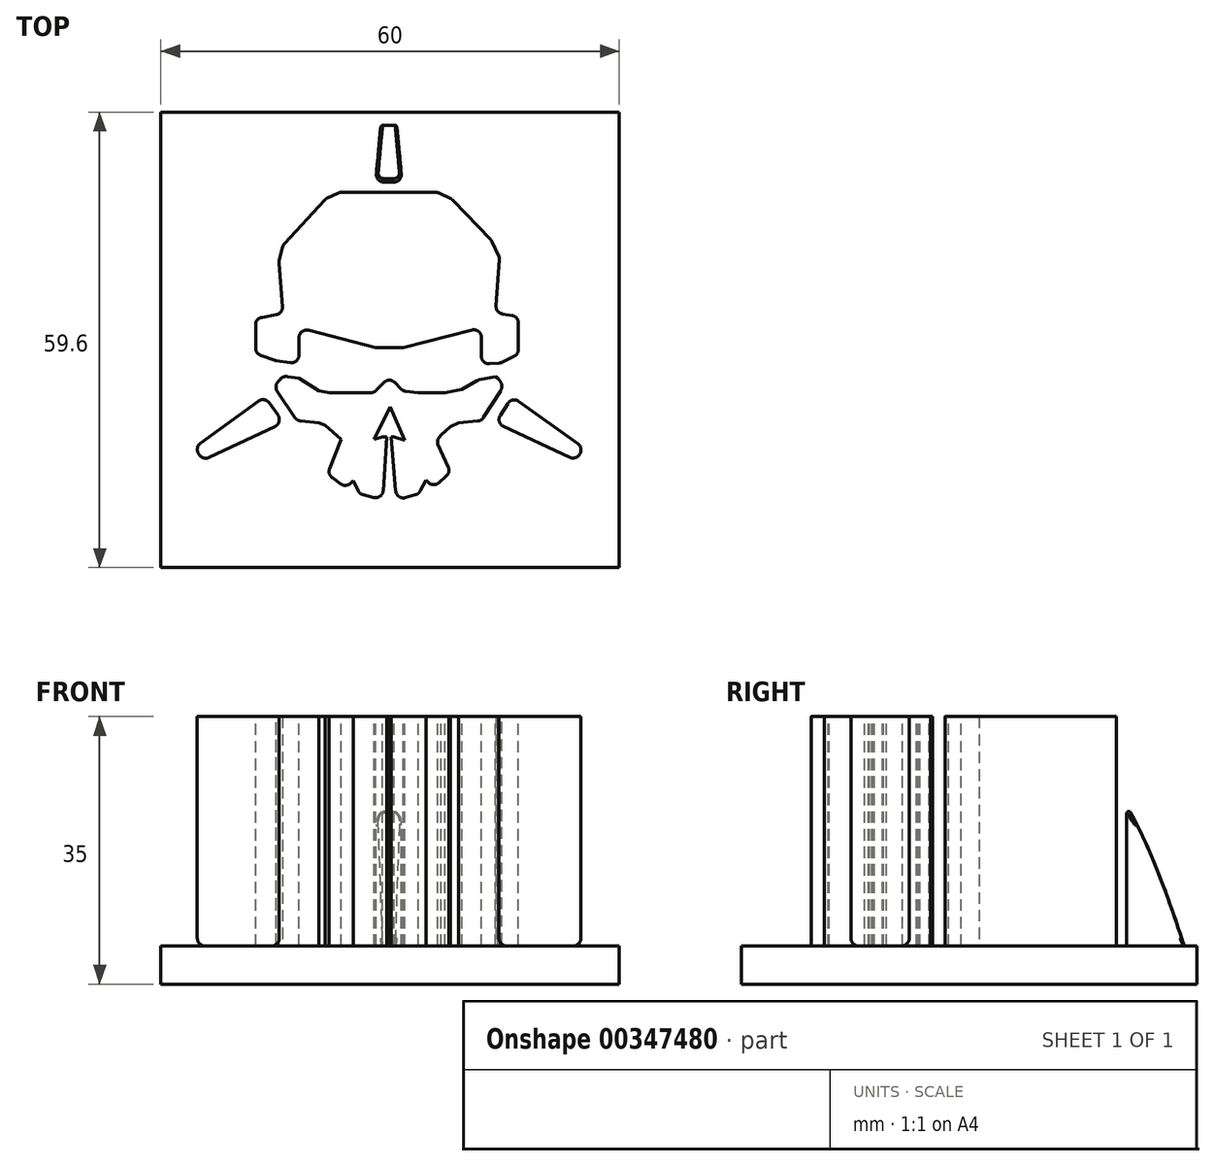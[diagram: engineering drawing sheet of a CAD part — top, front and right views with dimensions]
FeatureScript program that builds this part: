
annotation { "Feature Type Name" : "Feature", "Feature Type Description" : "" }
export const myFeature = defineFeature(function(context is Context, id is Id, definition is map)
    precondition{}
    {
        {
            var Q0;
            Q0=qCreatedBy(makeId("Front.planeOp"),FACE);
            var sketch = newSketch(context, id + "F0", { "sketchPlane" : qUnion([Q0])});
            skLineSegment(sketch, "E0", {"start": v(0, 0) * mm, "end": v(24, 0) * mm});
            skLineSegment(sketch, "E1", {"start": v(27, 5) * mm, "end": v(24, 0) * mm});
            skLineSegment(sketch, "E2", {"start": v(27, 5) * mm, "end": v(28.5, 5) * mm});
            skLineSegment(sketch, "E3", {"start": v(0, 35) * mm, "end": v(0, 0) * mm});
            skFitSpline(sketch, "E4", {"points": [v(0, 35) * mm, v(9.06, 34) * mm, v(13.03, 32.01) * mm, v(20.35, 24.23) * mm, v(28.5, 5) * mm], "startDerivative": vector(43.74, -2.76) * mm, "endDerivative": vector(20.52, -60.26) * mm});
            skSolve(sketch);
        }
        {
            var Q0;
            Q0=qSketchRegion(id+"F0",true);
            var Q1;
            Q1=sQuery(id+"F0.wireOp",EDGE,"E3");
            revolve(context, id + "F1", {"entities" : qUnion([Q0]), "axis" : qUnion([Q1]), "revolveType" : RevolveType.FULL});
        }
        {
            var Q0;
            Q0=qCreatedBy(makeId("Top.planeOp"),FACE);
            var sketch = newSketch(context, id + "F2", { "sketchPlane" : qUnion([Q0])});
            skCircle(sketch, "E5", {"center": v(0, 0) * mm, "radius": 5 * mm});
            skSolve(sketch);
        }
        {
            var Q0;
            Q0=qSketchRegion(id+"F2",true);
            extrude(context, id + "F3", {"entities" : qUnion([Q0]), "depth" : 32 * mm});
        }
        {
            var Q0;
            Q0=makeQuery(id+"F3.opExtrude","SWEPT_BODY",BODY,{"disambiguationData":[OSD([sQuery(id+"F2.wireOp",EDGE,"E5")])]});
            var Q1;
            Q1=makeQuery(id+"F1.opRevolve","SWEPT_BODY",BODY,{"disambiguationData":[OSD([sQuery(id+"F0.wireOp",EDGE,"E0"),sQuery(id+"F0.wireOp",EDGE,"E1"),sQuery(id+"F0.wireOp",EDGE,"E2"),sQuery(id+"F0.wireOp",EDGE,"3aklZLSy-hCqH-fZIi-s1VG-uW10MH76g0WD"),sQuery(id+"F0.wireOp",EDGE,"wuCtKPpf-We7b-kOsq-7vQO-teLjAkYNJH5X"),sQuery(id+"F0.wireOp",EDGE,"E3")])]});
            booleanBodies(context, id + "F4", {"operationType" : BooleanOperationType.SUBTRACTION, "tools" : qUnion([Q0]), "targets" : qUnion([Q1])});
        }
        {
            var Q0;
            Q0=qCreatedBy(makeId("Top.planeOp"),FACE);
            cPlane(context, id + "F5", {"entities" : qUnion([Q0]), "cplaneType" : CPlaneType.OFFSET, "offset" : 35 * mm, "width" : 150 * mm, "height" : 150 * mm});
        }
        {
            var Q0;
            Q0=qCreatedBy(id+"F5.planeOp",FACE);
            var sketch = newSketch(context, id + "F6", { "sketchPlane" : qUnion([Q0])});
            skLineSegment(sketch, "E6", {"start": v(-1.9, 20.95) * mm, "end": v(1.57, 20.95) * mm});
            skLineSegment(sketch, "E7", {"start": v(1.57, 20.95) * mm, "end": v(0.85, 28.83) * mm});
            skLineSegment(sketch, "E8", {"start": v(0.85, 28.83) * mm, "end": v(-1.17, 28.83) * mm});
            skLineSegment(sketch, "E9", {"start": v(-1.17, 28.83) * mm, "end": v(-1.9, 20.95) * mm});
            skLineSegment(sketch, "E10", {"start": v(-16.39, -7.1) * mm, "end": v(-14, -10.52) * mm});
            skLineSegment(sketch, "E11", {"start": v(-14, -10.52) * mm, "end": v(-24.43, -15.42) * mm});
            skLineSegment(sketch, "E12", {"start": v(-24.43, -15.42) * mm, "end": v(-25.63, -13.79) * mm});
            skLineSegment(sketch, "E13", {"start": v(-25.63, -13.79) * mm, "end": v(-16.39, -7.1) * mm});
            skLineSegment(sketch, "E14", {"start": v(16, -7.1) * mm, "end": v(13.8, -10.52) * mm});
            skLineSegment(sketch, "E15", {"start": v(13.8, -10.52) * mm, "end": v(24.28, -15.42) * mm});
            skLineSegment(sketch, "E16", {"start": v(24.28, -15.42) * mm, "end": v(25.36, -13.83) * mm});
            skLineSegment(sketch, "E17", {"start": v(25.36, -13.83) * mm, "end": v(16, -7.1) * mm});
            skLineSegment(sketch, "E18", {"start": v(-14, -4.39) * mm, "end": v(-11.93, -4.7) * mm});
            skLineSegment(sketch, "E19", {"start": v(-11.93, -4.7) * mm, "end": v(-9.33, -6.37) * mm});
            skLineSegment(sketch, "E20", {"start": v(-9.33, -6.37) * mm, "end": v(-7.9, -6.6) * mm});
            skLineSegment(sketch, "E21", {"start": v(-7.9, -6.6) * mm, "end": v(-4.54, -6.6) * mm});
            skLineSegment(sketch, "E22", {"start": v(-4.54, -6.6) * mm, "end": v(-2.11, -6.6) * mm});
            skLineSegment(sketch, "E23", {"start": v(-2.11, -6.6) * mm, "end": v(-0.46, -4.94) * mm});
            skLineSegment(sketch, "E24", {"start": v(-0.46, -4.94) * mm, "end": v(0.27, -4.94) * mm});
            skLineSegment(sketch, "E25", {"start": v(0.27, -4.94) * mm, "end": v(1.71, -6.37) * mm});
            skLineSegment(sketch, "E26", {"start": v(1.71, -6.37) * mm, "end": v(3.7, -6.6) * mm});
            skLineSegment(sketch, "E27", {"start": v(3.7, -6.6) * mm, "end": v(7.21, -6.6) * mm});
            skLineSegment(sketch, "E28", {"start": v(7.21, -6.6) * mm, "end": v(9.38, -6.15) * mm});
            skLineSegment(sketch, "E29", {"start": v(9.38, -6.15) * mm, "end": v(11.55, -4.94) * mm});
            skLineSegment(sketch, "E30", {"start": v(11.55, -4.94) * mm, "end": v(13.8, -4.5) * mm});
            skLineSegment(sketch, "E31", {"start": v(13.8, -4.5) * mm, "end": v(14.13, -4.7) * mm});
            skLineSegment(sketch, "E32", {"start": v(14.13, -4.7) * mm, "end": v(14.83, -5.76) * mm});
            skLineSegment(sketch, "E33", {"start": v(14.83, -5.76) * mm, "end": v(11.96, -10.26) * mm});
            skLineSegment(sketch, "E34", {"start": v(11.96, -10.26) * mm, "end": v(8.97, -10.52) * mm});
            skLineSegment(sketch, "E35", {"start": v(8.97, -10.52) * mm, "end": v(7.91, -11.03) * mm});
            skLineSegment(sketch, "E36", {"start": v(7.91, -11.03) * mm, "end": v(6.67, -12.1) * mm});
            skLineSegment(sketch, "E37", {"start": v(6.67, -12.1) * mm, "end": v(6.27, -12.72) * mm});
            skLineSegment(sketch, "E38", {"start": v(6.27, -12.72) * mm, "end": v(6.27, -13.33) * mm});
            skLineSegment(sketch, "E39", {"start": v(6.27, -13.33) * mm, "end": v(7.92, -17.05) * mm});
            skLineSegment(sketch, "E40", {"start": v(7.92, -17.05) * mm, "end": v(5.6, -19.03) * mm});
            skLineSegment(sketch, "E41", {"start": v(5.6, -19.03) * mm, "end": v(4.72, -18) * mm});
            skLineSegment(sketch, "E42", {"start": v(4.72, -18) * mm, "end": v(3.77, -19.83) * mm});
            skLineSegment(sketch, "E43", {"start": v(3.77, -19.83) * mm, "end": v(0.85, -20.66) * mm});
            skLineSegment(sketch, "E44", {"start": v(0.85, -20.66) * mm, "end": v(0.17, -12.4) * mm});
            skLineSegment(sketch, "E45", {"start": v(0.17, -12.4) * mm, "end": v(0.54, -12.37) * mm});
            skLineSegment(sketch, "E46", {"start": v(0.54, -12.37) * mm, "end": v(1.91, -12.83) * mm});
            skLineSegment(sketch, "E47", {"start": v(1.91, -12.83) * mm, "end": v(0, -8.41) * mm});
            skLineSegment(sketch, "E48", {"start": v(0, -8.41) * mm, "end": v(-2.11, -12.7) * mm});
            skLineSegment(sketch, "E49", {"start": v(-2.11, -12.7) * mm, "end": v(-0.97, -12.4) * mm});
            skLineSegment(sketch, "E50", {"start": v(-0.97, -12.4) * mm, "end": v(-0.46, -12.36) * mm});
            skLineSegment(sketch, "E51", {"start": v(-0.46, -12.36) * mm, "end": v(-0.97, -20.6) * mm});
            skLineSegment(sketch, "E52", {"start": v(-0.97, -20.6) * mm, "end": v(-3.99, -19.83) * mm});
            skLineSegment(sketch, "E53", {"start": v(-3.99, -19.83) * mm, "end": v(-4.79, -18.1) * mm});
            skLineSegment(sketch, "E54", {"start": v(-4.79, -18.1) * mm, "end": v(-5.8, -19) * mm});
            skLineSegment(sketch, "E55", {"start": v(-5.8, -19) * mm, "end": v(-8.2, -17.27) * mm});
            skLineSegment(sketch, "E56", {"start": v(-8.2, -17.27) * mm, "end": v(-6.4, -12.7) * mm});
            skLineSegment(sketch, "E57", {"start": v(-6.4, -12.7) * mm, "end": v(-8.47, -10.86) * mm});
            skLineSegment(sketch, "E58", {"start": v(-8.47, -10.86) * mm, "end": v(-9.33, -10.52) * mm});
            skLineSegment(sketch, "E59", {"start": v(-9.33, -10.52) * mm, "end": v(-12.14, -10.26) * mm});
            skLineSegment(sketch, "E60", {"start": v(-12.14, -10.26) * mm, "end": v(-15.2, -5.76) * mm});
            skLineSegment(sketch, "E61", {"start": v(-15.2, -5.76) * mm, "end": v(-14, -4.39) * mm});
            skLineSegment(sketch, "E62", {"start": v(-11.93, -2.85) * mm, "end": v(-14.9, -2.39) * mm});
            skLineSegment(sketch, "E63", {"start": v(-14.9, -2.39) * mm, "end": v(-17.6, -1.45) * mm});
            skLineSegment(sketch, "E64", {"start": v(-17.6, -1.45) * mm, "end": v(-17.6, 3.13) * mm});
            skLineSegment(sketch, "E65", {"start": v(-17.6, 3.13) * mm, "end": v(-14, 3.76) * mm});
            skLineSegment(sketch, "E66", {"start": v(-14, 3.76) * mm, "end": v(-14.56, 10.53) * mm});
            skLineSegment(sketch, "E67", {"start": v(-14.56, 10.53) * mm, "end": v(-14, 12.73) * mm});
            skLineSegment(sketch, "E68", {"start": v(-14, 12.73) * mm, "end": v(-8.4, 18.78) * mm});
            skLineSegment(sketch, "E69", {"start": v(-8.4, 18.78) * mm, "end": v(-6.64, 19.6) * mm});
            skLineSegment(sketch, "E70", {"start": v(-6.64, 19.6) * mm, "end": v(6.27, 19.6) * mm});
            skLineSegment(sketch, "E71", {"start": v(6.27, 19.6) * mm, "end": v(8.13, 18.7) * mm});
            skLineSegment(sketch, "E72", {"start": v(8.13, 18.7) * mm, "end": v(13.27, 13.32) * mm});
            skLineSegment(sketch, "E73", {"start": v(13.27, 13.32) * mm, "end": v(14.35, 11.03) * mm});
            skLineSegment(sketch, "E74", {"start": v(14.35, 11.03) * mm, "end": v(13.8, 3.84) * mm});
            skLineSegment(sketch, "E75", {"start": v(13.8, 3.84) * mm, "end": v(16.8, 3.38) * mm});
            skLineSegment(sketch, "E76", {"start": v(16.8, 3.38) * mm, "end": v(16.8, -1.57) * mm});
            skLineSegment(sketch, "E77", {"start": v(16.8, -1.57) * mm, "end": v(14.4, -2.7) * mm});
            skLineSegment(sketch, "E78", {"start": v(14.4, -2.7) * mm, "end": v(11.96, -2.9) * mm});
            skLineSegment(sketch, "E79", {"start": v(11.96, -2.9) * mm, "end": v(11.96, 1.93) * mm});
            skLineSegment(sketch, "E80", {"start": v(11.96, 1.93) * mm, "end": v(1.71, -0.7) * mm});
            skLineSegment(sketch, "E81", {"start": v(1.71, -0.7) * mm, "end": v(-1.9, -0.7) * mm});
            skLineSegment(sketch, "E82", {"start": v(-1.9, -0.7) * mm, "end": v(-11.93, 1.9) * mm});
            skLineSegment(sketch, "E83", {"start": v(-11.93, 1.9) * mm, "end": v(-11.93, -2.85) * mm});
            skSolve(sketch);
        }
        {
            var Q0;
            Q0 = qSketchRegion(id + "F6", true);
            extrude(context, id + "F7", {"entities" : qUnion([Q0]), "oppositeDirection" : true, "depth" : 30 * mm});
        }
        {
            var Q0;
            Q0=qCreatedBy(makeId("Right.planeOp"),FACE);
            var sketch = newSketch(context, id + "F8", { "sketchPlane" : qUnion([Q0])});
            skLineSegment(sketch, "E84.bottom", {"start": v(-29.48, 5) * mm, "end": v(30.12, 5) * mm});
            skLineSegment(sketch, "E84.top", {"start": v(-29.48, 0) * mm, "end": v(30.12, 0) * mm});
            skLineSegment(sketch, "E84.left", {"start": v(-29.48, 5) * mm, "end": v(-29.48, 0) * mm});
            skLineSegment(sketch, "E84.right", {"start": v(30.12, 5) * mm, "end": v(30.12, 0) * mm});
            skSolve(sketch);
        }
        {
            var Q0;
            Q0=makeQuery(id+"F7.opExtrude","SWEPT_EDGE",EDGE,{"disambiguationData":[OSD([sQuery(id+"F6.wireOp",EDGE,"E10"),sQuery(id+"F6.wireOp",EDGE,"E11")])]});
            var Q1;
            Q1=makeQuery(id+"F7.opExtrude","SWEPT_EDGE",EDGE,{"disambiguationData":[OSD([sQuery(id+"F6.wireOp",EDGE,"E59"),sQuery(id+"F6.wireOp",EDGE,"E60")])]});
            var Q2;
            Q2=makeQuery(id+"F7.opExtrude","SWEPT_EDGE",EDGE,{"disambiguationData":[OSD([sQuery(id+"F6.wireOp",EDGE,"E60"),sQuery(id+"F6.wireOp",EDGE,"E61")])]});
            var Q3;
            Q3=makeQuery(id+"F7.opExtrude","SWEPT_EDGE",EDGE,{"disambiguationData":[OSD([sQuery(id+"F6.wireOp",EDGE,"E33"),sQuery(id+"F6.wireOp",EDGE,"E34")])]});
            var Q4;
            Q4=makeQuery(id+"F7.opExtrude","SWEPT_EDGE",EDGE,{"disambiguationData":[OSD([sQuery(id+"F6.wireOp",EDGE,"E14"),sQuery(id+"F6.wireOp",EDGE,"E15")])]});
            var Q5;
            Q5=makeQuery(id+"F7.opExtrude","SWEPT_EDGE",EDGE,{"disambiguationData":[OSD([sQuery(id+"F6.wireOp",EDGE,"E39"),sQuery(id+"F6.wireOp",EDGE,"E40")])]});
            var Q6;
            Q6=makeQuery(id+"F7.opExtrude","SWEPT_EDGE",EDGE,{"disambiguationData":[OSD([sQuery(id+"F6.wireOp",EDGE,"E55"),sQuery(id+"F6.wireOp",EDGE,"E56")])]});
            var Q7;
            Q7=makeQuery(id+"F7.opExtrude","SWEPT_EDGE",EDGE,{"disambiguationData":[OSD([sQuery(id+"F6.wireOp",EDGE,"E51"),sQuery(id+"F6.wireOp",EDGE,"E52")])]});
            var Q8;
            Q8=makeQuery(id+"F7.opExtrude","SWEPT_EDGE",EDGE,{"disambiguationData":[OSD([sQuery(id+"F6.wireOp",EDGE,"E43"),sQuery(id+"F6.wireOp",EDGE,"E44")])]});
            var Q9;
            Q9=makeQuery(id+"F7.opExtrude","SWEPT_EDGE",EDGE,{"disambiguationData":[OSD([sQuery(id+"F6.wireOp",EDGE,"E42"),sQuery(id+"F6.wireOp",EDGE,"E43")])]});
            var Q10;
            Q10=makeQuery(id+"F7.opExtrude","SWEPT_EDGE",EDGE,{"disambiguationData":[OSD([sQuery(id+"F6.wireOp",EDGE,"E52"),sQuery(id+"F6.wireOp",EDGE,"E53")])]});
            var Q11;
            Q11=makeQuery(id+"F7.opExtrude","SWEPT_EDGE",EDGE,{"disambiguationData":[OSD([sQuery(id+"F6.wireOp",EDGE,"E54"),sQuery(id+"F6.wireOp",EDGE,"E55")])]});
            var Q12;
            Q12=makeQuery(id+"F7.opExtrude","SWEPT_EDGE",EDGE,{"disambiguationData":[OSD([sQuery(id+"F6.wireOp",EDGE,"E40"),sQuery(id+"F6.wireOp",EDGE,"E41")])]});
            var Q13;
            Q13=makeQuery(id+"F7.opExtrude","SWEPT_EDGE",EDGE,{"disambiguationData":[OSD([sQuery(id+"F6.wireOp",EDGE,"E32"),sQuery(id+"F6.wireOp",EDGE,"E33")])]});
            var Q14;
            Q14=makeQuery(id+"F7.opExtrude","SWEPT_EDGE",EDGE,{"disambiguationData":[OSD([sQuery(id+"F6.wireOp",EDGE,"E14"),sQuery(id+"F6.wireOp",EDGE,"E17")])]});
            var Q15;
            Q15=makeQuery(id+"F7.opExtrude","SWEPT_EDGE",EDGE,{"disambiguationData":[OSD([sQuery(id+"F6.wireOp",EDGE,"E10"),sQuery(id+"F6.wireOp",EDGE,"E13")])]});
            var Q16;
            Q16=makeQuery(id+"F7.opExtrude","SWEPT_EDGE",EDGE,{"disambiguationData":[OSD([sQuery(id+"F6.wireOp",EDGE,"E18"),sQuery(id+"F6.wireOp",EDGE,"E61")])]});
            var Q17;
            Q17=makeQuery(id+"F7.opExtrude","SWEPT_EDGE",EDGE,{"disambiguationData":[OSD([sQuery(id+"F6.wireOp",EDGE,"E22"),sQuery(id+"F6.wireOp",EDGE,"E23")])]});
            var Q18;
            Q18=makeQuery(id+"F7.opExtrude","SWEPT_EDGE",EDGE,{"disambiguationData":[OSD([sQuery(id+"F6.wireOp",EDGE,"E24"),sQuery(id+"F6.wireOp",EDGE,"E25")])]});
            var Q19;
            Q19=makeQuery(id+"F7.opExtrude","SWEPT_EDGE",EDGE,{"disambiguationData":[OSD([sQuery(id+"F6.wireOp",EDGE,"E25"),sQuery(id+"F6.wireOp",EDGE,"E26")])]});
            var Q20;
            Q20=makeQuery(id+"F7.opExtrude","SWEPT_EDGE",EDGE,{"disambiguationData":[OSD([sQuery(id+"F6.wireOp",EDGE,"E29"),sQuery(id+"F6.wireOp",EDGE,"E30")])]});
            var Q21;
            Q21=makeQuery(id+"F7.opExtrude","SWEPT_EDGE",EDGE,{"disambiguationData":[OSD([sQuery(id+"F6.wireOp",EDGE,"E6"),sQuery(id+"F6.wireOp",EDGE,"E7")])]});
            var Q22;
            Q22=makeQuery(id+"F7.opExtrude","SWEPT_EDGE",EDGE,{"disambiguationData":[OSD([sQuery(id+"F6.wireOp",EDGE,"E6"),sQuery(id+"F6.wireOp",EDGE,"E9")])]});
            var Q23;
            Q23=makeQuery(id+"F7.opExtrude","SWEPT_EDGE",EDGE,{"disambiguationData":[OSD([sQuery(id+"F6.wireOp",EDGE,"E69"),sQuery(id+"F6.wireOp",EDGE,"E70")])]});
            var Q24;
            Q24=makeQuery(id+"F7.opExtrude","SWEPT_EDGE",EDGE,{"disambiguationData":[OSD([sQuery(id+"F6.wireOp",EDGE,"E68"),sQuery(id+"F6.wireOp",EDGE,"E69")])]});
            var Q25;
            Q25=makeQuery(id+"F7.opExtrude","SWEPT_EDGE",EDGE,{"disambiguationData":[OSD([sQuery(id+"F6.wireOp",EDGE,"E70"),sQuery(id+"F6.wireOp",EDGE,"E71")])]});
            var Q26;
            Q26=makeQuery(id+"F7.opExtrude","SWEPT_EDGE",EDGE,{"disambiguationData":[OSD([sQuery(id+"F6.wireOp",EDGE,"E71"),sQuery(id+"F6.wireOp",EDGE,"E72")])]});
            var Q27;
            Q27=makeQuery(id+"F7.opExtrude","SWEPT_EDGE",EDGE,{"disambiguationData":[OSD([sQuery(id+"F6.wireOp",EDGE,"E67"),sQuery(id+"F6.wireOp",EDGE,"E68")])]});
            var Q28;
            Q28=makeQuery(id+"F7.opExtrude","SWEPT_EDGE",EDGE,{"disambiguationData":[OSD([sQuery(id+"F6.wireOp",EDGE,"E66"),sQuery(id+"F6.wireOp",EDGE,"E67")])]});
            var Q29;
            Q29=makeQuery(id+"F7.opExtrude","SWEPT_EDGE",EDGE,{"disambiguationData":[OSD([sQuery(id+"F6.wireOp",EDGE,"E65"),sQuery(id+"F6.wireOp",EDGE,"E66")])]});
            var Q30;
            Q30=makeQuery(id+"F7.opExtrude","SWEPT_EDGE",EDGE,{"disambiguationData":[OSD([sQuery(id+"F6.wireOp",EDGE,"E64"),sQuery(id+"F6.wireOp",EDGE,"E65")])]});
            var Q31;
            Q31=makeQuery(id+"F7.opExtrude","SWEPT_EDGE",EDGE,{"disambiguationData":[OSD([sQuery(id+"F6.wireOp",EDGE,"E63"),sQuery(id+"F6.wireOp",EDGE,"E64")])]});
            var Q32;
            Q32=makeQuery(id+"F7.opExtrude","SWEPT_EDGE",EDGE,{"disambiguationData":[OSD([sQuery(id+"F6.wireOp",EDGE,"E62"),sQuery(id+"F6.wireOp",EDGE,"E83")])]});
            var Q33;
            Q33=makeQuery(id+"F7.opExtrude","SWEPT_EDGE",EDGE,{"disambiguationData":[OSD([sQuery(id+"F6.wireOp",EDGE,"E82"),sQuery(id+"F6.wireOp",EDGE,"E83")])]});
            var Q34;
            Q34=makeQuery(id+"F7.opExtrude","SWEPT_EDGE",EDGE,{"disambiguationData":[OSD([sQuery(id+"F6.wireOp",EDGE,"E78"),sQuery(id+"F6.wireOp",EDGE,"E79")])]});
            var Q35;
            Q35=makeQuery(id+"F7.opExtrude","SWEPT_EDGE",EDGE,{"disambiguationData":[OSD([sQuery(id+"F6.wireOp",EDGE,"E77"),sQuery(id+"F6.wireOp",EDGE,"E78")])]});
            var Q36;
            Q36=makeQuery(id+"F7.opExtrude","SWEPT_EDGE",EDGE,{"disambiguationData":[OSD([sQuery(id+"F6.wireOp",EDGE,"E76"),sQuery(id+"F6.wireOp",EDGE,"E77")])]});
            var Q37;
            Q37=makeQuery(id+"F7.opExtrude","SWEPT_EDGE",EDGE,{"disambiguationData":[OSD([sQuery(id+"F6.wireOp",EDGE,"E75"),sQuery(id+"F6.wireOp",EDGE,"E76")])]});
            var Q38;
            Q38=makeQuery(id+"F7.opExtrude","SWEPT_EDGE",EDGE,{"disambiguationData":[OSD([sQuery(id+"F6.wireOp",EDGE,"E74"),sQuery(id+"F6.wireOp",EDGE,"E75")])]});
            var Q39;
            Q39=makeQuery(id+"F7.opExtrude","SWEPT_EDGE",EDGE,{"disambiguationData":[OSD([sQuery(id+"F6.wireOp",EDGE,"E73"),sQuery(id+"F6.wireOp",EDGE,"E74")])]});
            var Q40;
            Q40=makeQuery(id+"F7.opExtrude","SWEPT_EDGE",EDGE,{"disambiguationData":[OSD([sQuery(id+"F6.wireOp",EDGE,"E72"),sQuery(id+"F6.wireOp",EDGE,"E73")])]});
            var Q41;
            Q41=makeQuery(id+"F7.opExtrude","SWEPT_EDGE",EDGE,{"disambiguationData":[OSD([sQuery(id+"F6.wireOp",EDGE,"E79"),sQuery(id+"F6.wireOp",EDGE,"E80")])]});
            var Q42;
            Q42=makeQuery(id+"F7.opExtrude","SWEPT_EDGE",EDGE,{"disambiguationData":[OSD([sQuery(id+"F6.wireOp",EDGE,"E23"),sQuery(id+"F6.wireOp",EDGE,"E24")])]});
            var Q43;
            Q43=makeQuery(id+"F7.opExtrude","SWEPT_EDGE",EDGE,{"disambiguationData":[OSD([sQuery(id+"F6.wireOp",EDGE,"E11"),sQuery(id+"F6.wireOp",EDGE,"E12")])]});
            var Q44;
            Q44=makeQuery(id+"F7.opExtrude","SWEPT_EDGE",EDGE,{"disambiguationData":[OSD([sQuery(id+"F6.wireOp",EDGE,"E12"),sQuery(id+"F6.wireOp",EDGE,"E13")])]});
            var Q45;
            Q45=makeQuery(id+"F7.opExtrude","SWEPT_EDGE",EDGE,{"disambiguationData":[OSD([sQuery(id+"F6.wireOp",EDGE,"E15"),sQuery(id+"F6.wireOp",EDGE,"E16")])]});
            var Q46;
            Q46=makeQuery(id+"F7.opExtrude","SWEPT_EDGE",EDGE,{"disambiguationData":[OSD([sQuery(id+"F6.wireOp",EDGE,"E16"),sQuery(id+"F6.wireOp",EDGE,"E17")])]});
            var Q47;
            Q47=makeQuery(id+"F7.opExtrude","SWEPT_EDGE",EDGE,{"disambiguationData":[OSD([sQuery(id+"F6.wireOp",EDGE,"E8"),sQuery(id+"F6.wireOp",EDGE,"E9")])]});
            var Q48;
            Q48=makeQuery(id+"F7.opExtrude","SWEPT_EDGE",EDGE,{"disambiguationData":[OSD([sQuery(id+"F6.wireOp",EDGE,"E7"),sQuery(id+"F6.wireOp",EDGE,"E8")])]});
            fillet(context, id + "F9", {"entities" : qUnion([Q0, Q1, Q2, Q3, Q4, Q5, Q6, Q7, Q8, Q9, Q10, Q11, Q12, Q13, Q14, Q15, Q16, Q17, Q18, Q19, Q20, Q21, Q22, Q23, Q24, Q25, Q26, Q27, Q28, Q29, Q30, Q31, Q32, Q33, Q34, Q35, Q36, Q37, Q38, Q39, Q40, Q41, Q42, Q43, Q44, Q45, Q46, Q47, Q48]), "radius" : 1 * mm, "tangentPropagation" : true, "allowEdgeOverflow" : false});
        }
        {
            var Q0;
            Q0 = qSketchRegion(id + "F8", true);
            extrude(context, id + "F10", {"entities" : qUnion([Q0]), "endBound" : BoundingType.SYMMETRIC, "oppositeDirection" : true, "depth" : 60 * mm});
        }
        {
            var Q0;
            Q0=makeQuery(id+"F1.opRevolve","SWEPT_BODY",BODY,{"disambiguationData":[OSD([sQuery(id+"F0.wireOp",EDGE,"E0"),sQuery(id+"F0.wireOp",EDGE,"E1"),sQuery(id+"F0.wireOp",EDGE,"E2"),sQuery(id+"F0.wireOp",EDGE,"3aklZLSy-hCqH-fZIi-s1VG-uW10MH76g0WD"),sQuery(id+"F0.wireOp",EDGE,"wuCtKPpf-We7b-kOsq-7vQO-teLjAkYNJH5X"),sQuery(id+"F0.wireOp",EDGE,"E3")])]});
            var Q1;
            Q1=makeQuery(id+"F7.opExtrude","SWEPT_BODY",BODY,{"disambiguationData":[OSD([sQuery(id+"F6.wireOp",EDGE,"E6"),sQuery(id+"F6.wireOp",EDGE,"E7"),sQuery(id+"F6.wireOp",EDGE,"E8"),sQuery(id+"F6.wireOp",EDGE,"E9")])]});
            booleanBodies(context, id + "F11", {"operationType" : BooleanOperationType.INTERSECTION, "tools" : qUnion([Q0, Q1])});
        }
        {
            var Q0;
            {var subQ0=sQuery(id+"F0.wireOp",EDGE,"E2");var subQ1=sQuery(id+"F6.wireOp",EDGE,"E16");var subQ2=sQuery(id+"F0.wireOp",EDGE,"E4");Q0=makeQuery(id+"F11.opBoolean","SPLIT",EDGE,{"disambiguationData":[TD([makeQuery(id+"F9.opFillet","BLEND_FACE",FACE,{"disambiguationData":[OSD([sQuery(id+"F6.wireOp",EDGE,"E15"),subQ1])]})])],"derivedFrom":makeQuery(id+"F1.opRevolve","SWEPT_EDGE",EDGE,{"disambiguationData":[OSD([subQ0,subQ2])]})});}
            var Q1;
            Q1=makeQuery(id+"F11.opBoolean","INTERSECT",EDGE,{"derivedFrom":[makeQuery(id+"F1.opRevolve","SWEPT_FACE",FACE,{"disambiguationData":[OSD([sQuery(id+"F0.wireOp",EDGE,"E4")])]}),makeQuery(id+"F7.opExtrude","SWEPT_FACE",FACE,{"disambiguationData":[OSD([sQuery(id+"F6.wireOp",EDGE,"E14")])]})]});
            var Q2;
            {var subQ0=sQuery(id+"F0.wireOp",EDGE,"E2");var subQ1=sQuery(id+"F0.wireOp",EDGE,"E4");var subQ2=sQuery(id+"F6.wireOp",EDGE,"E12");Q2=makeQuery(id+"F11.opBoolean","SPLIT",EDGE,{"disambiguationData":[TD([makeQuery(id+"F9.opFillet","BLEND_FACE",FACE,{"disambiguationData":[OSD([sQuery(id+"F6.wireOp",EDGE,"E11"),subQ2])]})])],"derivedFrom":makeQuery(id+"F1.opRevolve","SWEPT_EDGE",EDGE,{"disambiguationData":[OSD([subQ0,subQ1])]})});}
            var Q3;
            Q3=makeQuery(id+"F11.opBoolean","INTERSECT",EDGE,{"derivedFrom":[makeQuery(id+"F1.opRevolve","SWEPT_FACE",FACE,{"disambiguationData":[OSD([sQuery(id+"F0.wireOp",EDGE,"E4")])]}),makeQuery(id+"F7.opExtrude","SWEPT_FACE",FACE,{"disambiguationData":[OSD([sQuery(id+"F6.wireOp",EDGE,"E10")])]})]});
            var Q4;
            {var subQ0=sQuery(id+"F0.wireOp",EDGE,"E2");var subQ1=sQuery(id+"F0.wireOp",EDGE,"E4");var subQ2=sQuery(id+"F6.wireOp",EDGE,"E8");Q4=makeQuery(id+"F11.opBoolean","SPLIT",EDGE,{"disambiguationData":[TD([makeQuery(id+"F9.opFillet","BLEND_FACE",FACE,{"disambiguationData":[OSD([sQuery(id+"F6.wireOp",EDGE,"E7"),subQ2])]})])],"derivedFrom":makeQuery(id+"F1.opRevolve","SWEPT_EDGE",EDGE,{"disambiguationData":[OSD([subQ0,subQ1])]})});}
            var Q5;
            Q5=makeQuery(id+"F11.opBoolean","INTERSECT",EDGE,{"derivedFrom":[makeQuery(id+"F1.opRevolve","SWEPT_FACE",FACE,{"disambiguationData":[OSD([sQuery(id+"F0.wireOp",EDGE,"E4")])]}),makeQuery(id+"F7.opExtrude","SWEPT_FACE",FACE,{"disambiguationData":[OSD([sQuery(id+"F6.wireOp",EDGE,"E6")])]})]});
            var Q6;
            {var subQ16=sQuery(id+"F6.wireOp",EDGE,"E62");Q6=makeQuery(id+"F11.opBoolean","SPLIT",FACE,{"disambiguationData":[TD([makeQuery(id+"F7.opExtrude","SWEPT_FACE",FACE,{"disambiguationData":[OSD([subQ16])]})])],"derivedFrom":makeQuery(id+"F1.opRevolve","SWEPT_FACE",FACE,{"disambiguationData":[OSD([sQuery(id+"F0.wireOp",EDGE,"E4")])]})});}
            var Q7;
            {var subQ16=sQuery(id+"F6.wireOp",EDGE,"E18");Q7=makeQuery(id+"F11.opBoolean","SPLIT",FACE,{"disambiguationData":[TD([makeQuery(id+"F7.opExtrude","SWEPT_FACE",FACE,{"disambiguationData":[OSD([subQ16])]})])],"derivedFrom":makeQuery(id+"F1.opRevolve","SWEPT_FACE",FACE,{"disambiguationData":[OSD([sQuery(id+"F0.wireOp",EDGE,"E4")])]})});}
            fillet(context, id + "F12", {"entities" : qUnion([Q0, Q1, Q2, Q3, Q4, Q5, Q6, Q7]), "radius" : 0.25 * mm, "tangentPropagation" : true, "allowEdgeOverflow" : false});
        }
        {
            var Q0;
            {var subQ0=sQuery(id+"F6.wireOp",EDGE,"E11");Q0=makeQuery(id+"F11.opBoolean","SPLIT",EDGE,{"disambiguationData":[topologyDisambiguationEdgeConnected([makeQuery(id+"F10.opExtrude","SWEPT_FACE",FACE,{"disambiguationData":[OSD([sQuery(id+"F8.wireOp",EDGE,"E84.bottom")])]})])],"derivedFrom":makeQuery(id+"F7.opExtrude","CAP_EDGE",EDGE,{"disambiguationData":[OSD([subQ0])],"isStart":false})});}
            var Q1;
            {var subQ0=sQuery(id+"F6.wireOp",EDGE,"E15");Q1=makeQuery(id+"F11.opBoolean","SPLIT",EDGE,{"disambiguationData":[topologyDisambiguationEdgeConnected([makeQuery(id+"F10.opExtrude","SWEPT_FACE",FACE,{"disambiguationData":[OSD([sQuery(id+"F8.wireOp",EDGE,"E84.bottom")])]})])],"derivedFrom":makeQuery(id+"F7.opExtrude","CAP_EDGE",EDGE,{"disambiguationData":[OSD([subQ0])],"isStart":false})});}
            var Q2;
            {var subQ0=sQuery(id+"F6.wireOp",EDGE,"E9");Q2=makeQuery(id+"F11.opBoolean","SPLIT",EDGE,{"disambiguationData":[topologyDisambiguationEdgeConnected([makeQuery(id+"F10.opExtrude","SWEPT_FACE",FACE,{"disambiguationData":[OSD([sQuery(id+"F8.wireOp",EDGE,"E84.bottom")])]})])],"derivedFrom":makeQuery(id+"F7.opExtrude","CAP_EDGE",EDGE,{"disambiguationData":[OSD([subQ0])],"isStart":false})});}
            fillet(context, id + "F13", {"entities" : qUnion([Q0, Q1, Q2]), "radius" : 1 * mm, "tangentPropagation" : true, "allowEdgeOverflow" : false});
        }
    });
